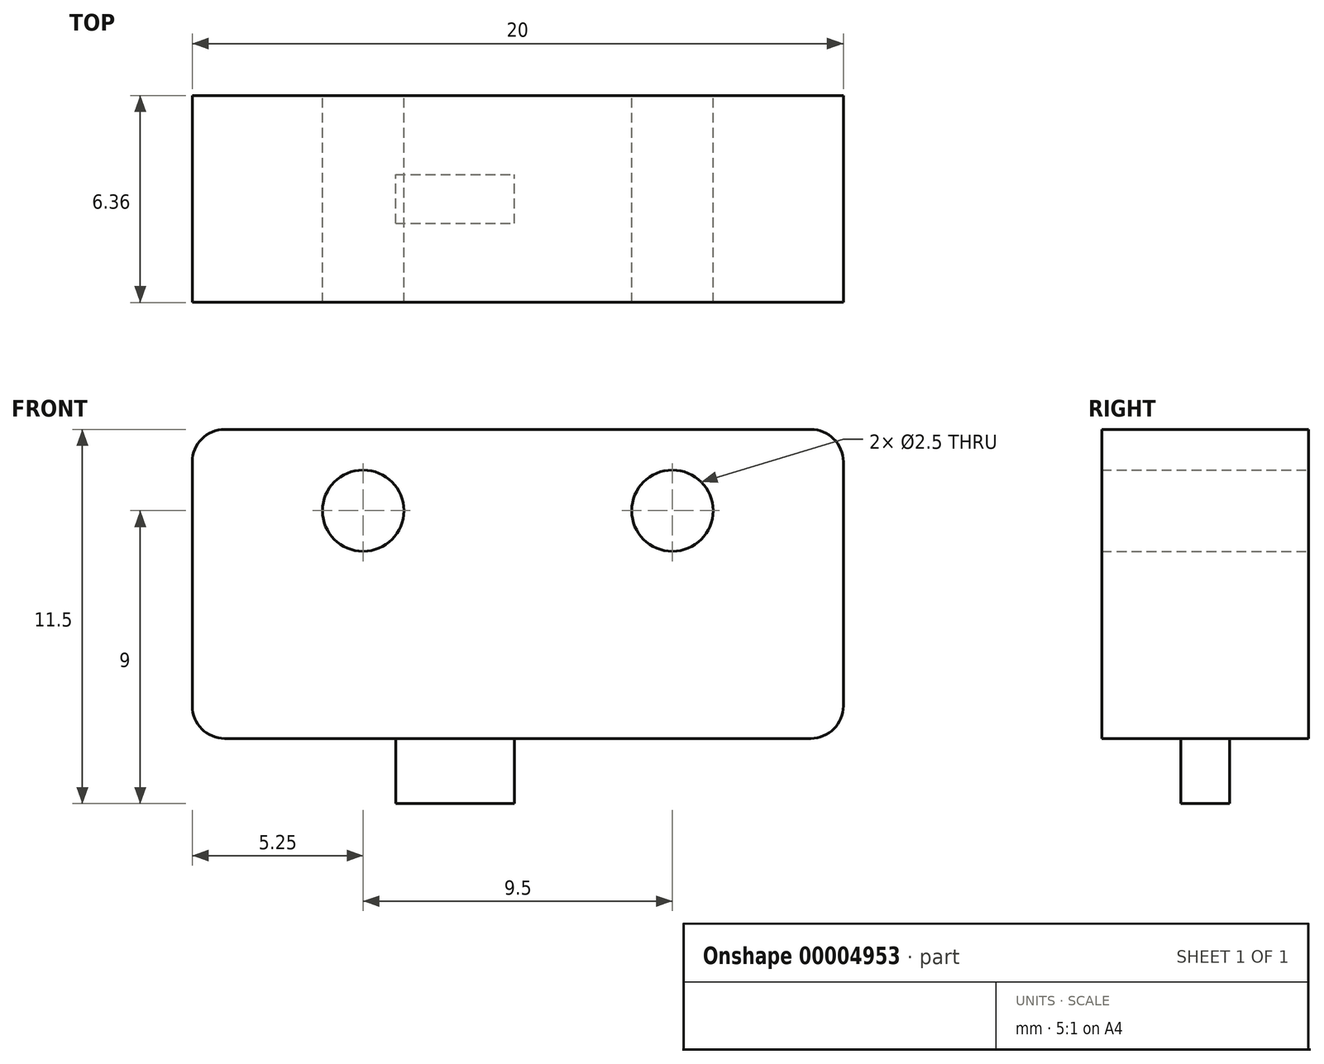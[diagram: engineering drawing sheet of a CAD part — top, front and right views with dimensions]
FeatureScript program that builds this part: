
annotation { "Feature Type Name" : "Feature", "Feature Type Description" : "" }
export const myFeature = defineFeature(function(context is Context, id is Id, definition is map)
    precondition{}
    {
        {
            var Q0;
            Q0=qCreatedBy(makeId("Front.planeOp"),FACE);
            var sketch = newSketch(context, id + "F0", { "sketchPlane" : qUnion([Q0])});
            skLineSegment(sketch, "E0", {"start": v(0, 0) * mm, "end": v(0, 9.31) * mm, "construction": true});
            skLineSegment(sketch, "E1.rect.bottom", {"start": v(10, 4.75) * mm, "end": v(-10, 4.75) * mm});
            skLineSegment(sketch, "E1.rect.top", {"start": v(10, -4.75) * mm, "end": v(-10, -4.75) * mm});
            skLineSegment(sketch, "E1.rect.left", {"start": v(10, 4.75) * mm, "end": v(10, -4.75) * mm});
            skLineSegment(sketch, "E1.rect.right", {"start": v(-10, 4.75) * mm, "end": v(-10, -4.75) * mm});
            skPoint(sketch, "E1.rect.middle", {"position": v(0, 0) * mm});
            skCircle(sketch, "E2", {"center": v(-4.75, 2.25) * mm, "radius": 1.25 * mm});
            skCircle(sketch, "E3.0.MirrorC", {"center": v(4.75, 2.25) * mm, "radius": 1.25 * mm});
            skSolve(sketch);
        }
        {
            var Q0;
            Q0 = qSketchRegion(id + "F0", true);
            extrude(context, id + "F1", {"entities" : qUnion([Q0]), "depth" : 6.35 * mm, "symmetric" : true});
        }
        {
            var Q0;
            Q0=qCreatedBy(makeId("Front.planeOp"),FACE);
            var sketch = newSketch(context, id + "F2", { "sketchPlane" : qUnion([Q0])});
            skLineSegment(sketch, "E4.0", {"start": v(10, -4.75) * mm, "end": v(-10, -4.75) * mm, "construction": true});
            skLineSegment(sketch, "E5.bottom", {"start": v(-3.75, -4.75) * mm, "end": v(-0.1, -4.75) * mm});
            skLineSegment(sketch, "E5.top", {"start": v(-3.75, -6.75) * mm, "end": v(-0.1, -6.75) * mm});
            skLineSegment(sketch, "E5.left", {"start": v(-3.75, -4.75) * mm, "end": v(-3.75, -6.75) * mm});
            skLineSegment(sketch, "E5.right", {"start": v(-0.1, -4.75) * mm, "end": v(-0.1, -6.75) * mm});
            skSolve(sketch);
        }
        {
            var Q0;
            Q0 = qSketchRegion(id + "F2", true);
            extrude(context, id + "F3", {"entities" : qUnion([Q0]), "operationType" : NewBodyOperationType.ADD, "depth" : 1.5 * mm, "symmetric" : true});
        }
        {
            var Q0;
            Q0=makeQuery(id+"F1.opExtrude","SWEPT_EDGE",EDGE,{"disambiguationData":[OSD([sQuery(id+"F0.wireOp",EDGE,"E1.rect.bottom"),sQuery(id+"F0.wireOp",EDGE,"E1.rect.right")])]});
            var Q1;
            Q1=makeQuery(id+"F1.opExtrude","SWEPT_EDGE",EDGE,{"disambiguationData":[OSD([sQuery(id+"F0.wireOp",EDGE,"E1.rect.top"),sQuery(id+"F0.wireOp",EDGE,"E1.rect.right")])]});
            var Q2;
            Q2=makeQuery(id+"F1.opExtrude","SWEPT_EDGE",EDGE,{"disambiguationData":[OSD([sQuery(id+"F0.wireOp",EDGE,"E1.rect.top"),sQuery(id+"F0.wireOp",EDGE,"E1.rect.left")])]});
            var Q3;
            Q3=makeQuery(id+"F1.opExtrude","SWEPT_EDGE",EDGE,{"disambiguationData":[OSD([sQuery(id+"F0.wireOp",EDGE,"E1.rect.bottom"),sQuery(id+"F0.wireOp",EDGE,"E1.rect.left")])]});
            fillet(context, id + "F4", {"entities" : qUnion([Q0, Q1, Q2, Q3]), "radius" : 1 * mm, "tangentPropagation" : true, "allowEdgeOverflow" : false});
        }
    });
